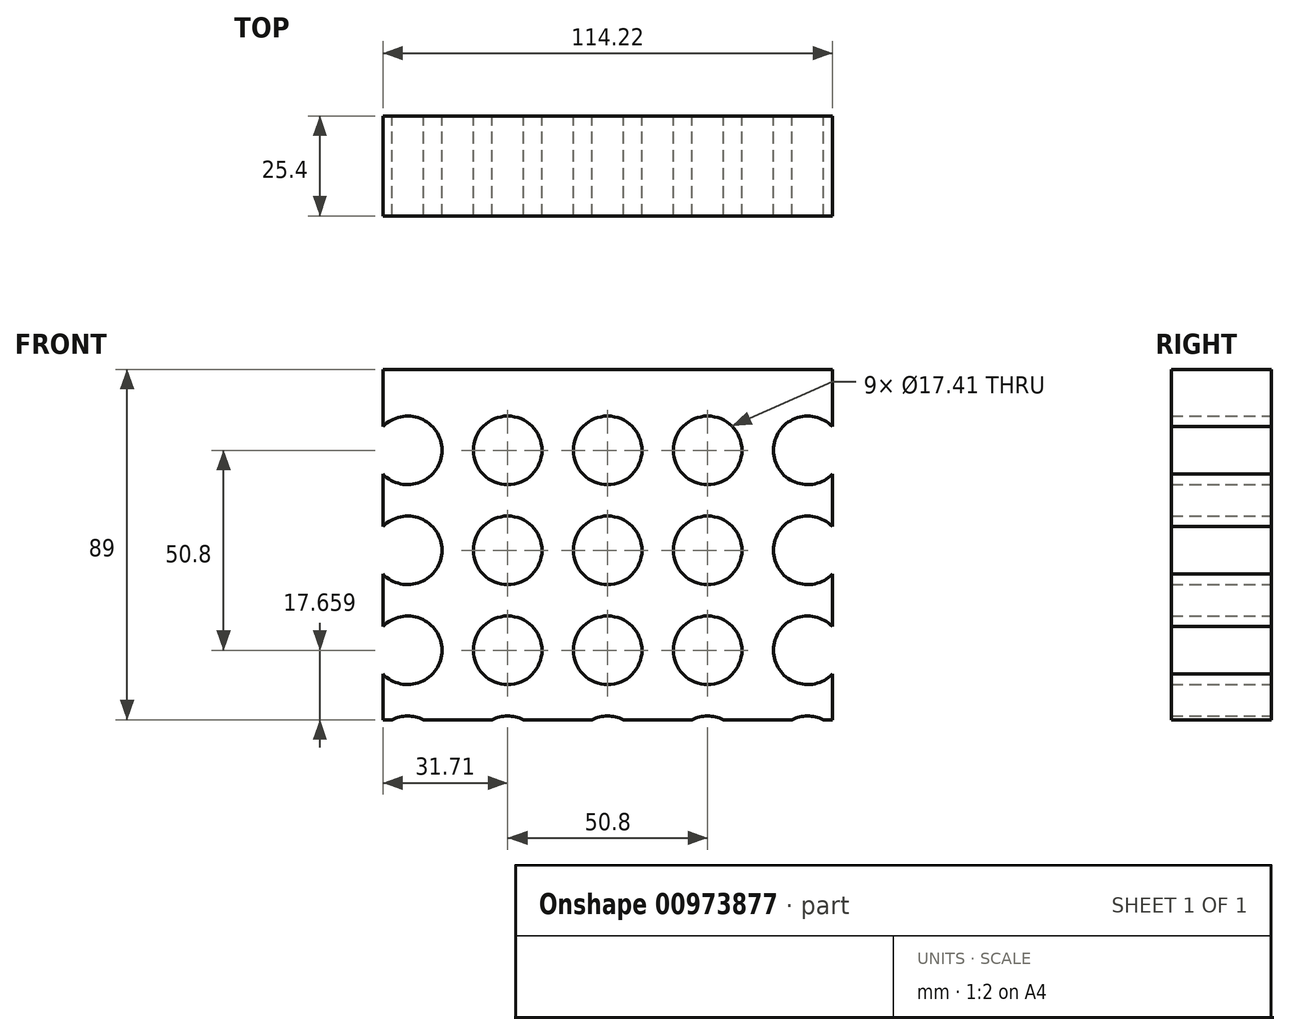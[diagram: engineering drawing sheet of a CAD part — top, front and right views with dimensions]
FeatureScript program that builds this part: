
annotation { "Feature Type Name" : "Feature", "Feature Type Description" : "" }
export const myFeature = defineFeature(function(context is Context, id is Id, definition is map)
    precondition{}
    {
        {
            var Q0;
            Q0=qCreatedBy(makeId("Front.planeOp"),FACE);
            var sketch = newSketch(context, id + "F0", { "sketchPlane" : qUnion([Q0])});
            skLineSegment(sketch, "E0.bottom", {"start": v(57.1, 44.5) * mm, "end": v(-57.1, 44.5) * mm});
            skLineSegment(sketch, "E0.top", {"start": v(57.1, -44.5) * mm, "end": v(-57.1, -44.5) * mm});
            skLineSegment(sketch, "E0.left", {"start": v(57.1, 44.5) * mm, "end": v(57.1, -44.5) * mm});
            skLineSegment(sketch, "E0.right", {"start": v(-57.1, 44.5) * mm, "end": v(-57.1, -44.5) * mm});
            skPoint(sketch, "E0.middle", {"position": v(0, 0) * mm});
            skCircle(sketch, "E1", {"center": v(-25.4, 23.96) * mm, "radius": 8.7 * mm});
            skCircle(sketch, "E2.1.0.0", {"center": v(0, 23.96) * mm, "radius": 8.7 * mm});
            skCircle(sketch, "E2.2.0.0", {"center": v(25.4, 23.96) * mm, "radius": 8.7 * mm});
            skLineSegment(sketch, "E2.direction1", {"start": v(-25.4, 23.96) * mm, "end": v(0, 23.96) * mm, "construction": true});
            skCircle(sketch, "E3.0.3.0", {"center": v(50.8, 23.96) * mm, "radius": 8.7 * mm});
            skCircle(sketch, "E3.0.4.0", {"center": v(76.2, 23.96) * mm, "radius": 8.7 * mm});
            skCircle(sketch, "E3.0.5.0", {"center": v(101.6, 23.96) * mm, "radius": 8.7 * mm});
            skCircle(sketch, "E3.0.6.0", {"center": v(127, 23.96) * mm, "radius": 8.7 * mm});
            skCircle(sketch, "E3.0.7.0", {"center": v(152.4, 23.96) * mm, "radius": 8.7 * mm});
            skCircle(sketch, "E3.0.8.0", {"center": v(177.8, 23.96) * mm, "radius": 8.7 * mm});
            skCircle(sketch, "E3.0.9.0", {"center": v(203.2, 23.96) * mm, "radius": 8.7 * mm});
            skCircle(sketch, "E3.0.10.0", {"center": v(228.6, 23.96) * mm, "radius": 8.7 * mm});
            skCircle(sketch, "E3.0.11.0", {"center": v(254, 23.96) * mm, "radius": 8.7 * mm});
            skCircle(sketch, "E3.0.12.0", {"center": v(279.4, 23.96) * mm, "radius": 8.7 * mm});
            skCircle(sketch, "E3.0.13.0", {"center": v(304.8, 23.96) * mm, "radius": 8.7 * mm});
            skCircle(sketch, "E3.0.14.0", {"center": v(330.2, 23.96) * mm, "radius": 8.7 * mm});
            skLineSegment(sketch, "E4.0.1.0", {"start": v(57.1, 19.1) * mm, "end": v(57.1, -69.9) * mm});
            skCircle(sketch, "E4.0.1.1", {"center": v(-25.4, -1.44) * mm, "radius": 8.7 * mm});
            skCircle(sketch, "E4.0.1.2", {"center": v(0, -1.44) * mm, "radius": 8.7 * mm});
            skPoint(sketch, "E4.0.1.3", {"position": v(0, -25.4) * mm});
            skCircle(sketch, "E4.0.1.4", {"center": v(25.4, -1.44) * mm, "radius": 8.7 * mm});
            skCircle(sketch, "E4.0.1.5", {"center": v(50.8, -1.44) * mm, "radius": 8.7 * mm});
            skCircle(sketch, "E4.0.1.6", {"center": v(76.2, -1.44) * mm, "radius": 8.7 * mm});
            skCircle(sketch, "E4.0.1.7", {"center": v(101.6, -1.44) * mm, "radius": 8.7 * mm});
            skCircle(sketch, "E4.0.1.8", {"center": v(127, -1.44) * mm, "radius": 8.7 * mm});
            skLineSegment(sketch, "E4.0.2.0", {"start": v(57.1, -6.3) * mm, "end": v(57.1, -95.3) * mm});
            skCircle(sketch, "E4.0.2.1", {"center": v(-25.4, -26.84) * mm, "radius": 8.7 * mm});
            skCircle(sketch, "E4.0.2.2", {"center": v(0, -26.84) * mm, "radius": 8.7 * mm});
            skPoint(sketch, "E4.0.2.3", {"position": v(0, -50.8) * mm});
            skCircle(sketch, "E4.0.2.4", {"center": v(25.4, -26.84) * mm, "radius": 8.7 * mm});
            skCircle(sketch, "E4.0.2.5", {"center": v(50.8, -26.84) * mm, "radius": 8.7 * mm});
            skCircle(sketch, "E4.0.2.6", {"center": v(76.2, -26.84) * mm, "radius": 8.7 * mm});
            skCircle(sketch, "E4.0.2.7", {"center": v(101.6, -26.84) * mm, "radius": 8.7 * mm});
            skCircle(sketch, "E4.0.2.8", {"center": v(127, -26.84) * mm, "radius": 8.7 * mm});
            skLineSegment(sketch, "E4.0.3.0", {"start": v(57.1, -31.7) * mm, "end": v(57.1, -120.7) * mm});
            skCircle(sketch, "E4.0.3.1", {"center": v(-25.4, -52.24) * mm, "radius": 8.7 * mm});
            skCircle(sketch, "E4.0.3.2", {"center": v(0, -52.24) * mm, "radius": 8.7 * mm});
            skPoint(sketch, "E4.0.3.3", {"position": v(0, -76.2) * mm});
            skCircle(sketch, "E4.0.3.4", {"center": v(25.4, -52.24) * mm, "radius": 8.7 * mm});
            skCircle(sketch, "E4.0.3.5", {"center": v(50.8, -52.24) * mm, "radius": 8.7 * mm});
            skCircle(sketch, "E4.0.3.6", {"center": v(76.2, -52.24) * mm, "radius": 8.7 * mm});
            skCircle(sketch, "E4.0.3.7", {"center": v(101.6, -52.24) * mm, "radius": 8.7 * mm});
            skCircle(sketch, "E4.0.3.8", {"center": v(127, -52.24) * mm, "radius": 8.7 * mm});
            skLineSegment(sketch, "E4.0.4.0", {"start": v(57.1, -57.1) * mm, "end": v(57.1, -146.1) * mm});
            skCircle(sketch, "E4.0.4.1", {"center": v(-25.4, -77.64) * mm, "radius": 8.7 * mm});
            skCircle(sketch, "E4.0.4.2", {"center": v(0, -77.64) * mm, "radius": 8.7 * mm});
            skPoint(sketch, "E4.0.4.3", {"position": v(0, -101.6) * mm});
            skCircle(sketch, "E4.0.4.4", {"center": v(25.4, -77.64) * mm, "radius": 8.7 * mm});
            skCircle(sketch, "E4.0.4.5", {"center": v(50.8, -77.64) * mm, "radius": 8.7 * mm});
            skCircle(sketch, "E4.0.4.6", {"center": v(76.2, -77.64) * mm, "radius": 8.7 * mm});
            skCircle(sketch, "E4.0.4.7", {"center": v(101.6, -77.64) * mm, "radius": 8.7 * mm});
            skCircle(sketch, "E4.0.4.8", {"center": v(127, -77.64) * mm, "radius": 8.7 * mm});
            skLineSegment(sketch, "E4.1.0.0", {"start": v(31.7, 44.5) * mm, "end": v(31.7, -44.5) * mm});
            skCircle(sketch, "E4.1.0.1", {"center": v(-50.8, 23.96) * mm, "radius": 8.7 * mm});
            skPoint(sketch, "E4.1.0.3", {"position": v(-25.4, 0) * mm});
            skLineSegment(sketch, "E4.1.1.0", {"start": v(31.7, 19.1) * mm, "end": v(31.7, -69.9) * mm});
            skCircle(sketch, "E4.1.1.1", {"center": v(-50.8, -1.44) * mm, "radius": 8.7 * mm});
            skCircle(sketch, "E4.1.1.2", {"center": v(-25.4, -1.44) * mm, "radius": 8.7 * mm});
            skPoint(sketch, "E4.1.1.3", {"position": v(-25.4, -25.4) * mm});
            skCircle(sketch, "E4.1.1.4", {"center": v(0, -1.44) * mm, "radius": 8.7 * mm});
            skCircle(sketch, "E4.1.1.5", {"center": v(25.4, -1.44) * mm, "radius": 8.7 * mm});
            skCircle(sketch, "E4.1.1.6", {"center": v(50.8, -1.44) * mm, "radius": 8.7 * mm});
            skCircle(sketch, "E4.1.1.7", {"center": v(76.2, -1.44) * mm, "radius": 8.7 * mm});
            skCircle(sketch, "E4.1.1.8", {"center": v(101.6, -1.44) * mm, "radius": 8.7 * mm});
            skLineSegment(sketch, "E4.1.2.0", {"start": v(31.7, -6.3) * mm, "end": v(31.7, -95.3) * mm});
            skCircle(sketch, "E4.1.2.1", {"center": v(-50.8, -26.84) * mm, "radius": 8.7 * mm});
            skCircle(sketch, "E4.1.2.2", {"center": v(-25.4, -26.84) * mm, "radius": 8.7 * mm});
            skPoint(sketch, "E4.1.2.3", {"position": v(-25.4, -50.8) * mm});
            skCircle(sketch, "E4.1.2.4", {"center": v(0, -26.84) * mm, "radius": 8.7 * mm});
            skCircle(sketch, "E4.1.2.5", {"center": v(25.4, -26.84) * mm, "radius": 8.7 * mm});
            skCircle(sketch, "E4.1.2.6", {"center": v(50.8, -26.84) * mm, "radius": 8.7 * mm});
            skCircle(sketch, "E4.1.2.7", {"center": v(76.2, -26.84) * mm, "radius": 8.7 * mm});
            skCircle(sketch, "E4.1.2.8", {"center": v(101.6, -26.84) * mm, "radius": 8.7 * mm});
            skLineSegment(sketch, "E4.1.3.0", {"start": v(31.7, -31.7) * mm, "end": v(31.7, -120.7) * mm});
            skCircle(sketch, "E4.1.3.1", {"center": v(-50.8, -52.24) * mm, "radius": 8.7 * mm});
            skCircle(sketch, "E4.1.3.2", {"center": v(-25.4, -52.24) * mm, "radius": 8.7 * mm});
            skPoint(sketch, "E4.1.3.3", {"position": v(-25.4, -76.2) * mm});
            skCircle(sketch, "E4.1.3.4", {"center": v(0, -52.24) * mm, "radius": 8.7 * mm});
            skCircle(sketch, "E4.1.3.5", {"center": v(25.4, -52.24) * mm, "radius": 8.7 * mm});
            skCircle(sketch, "E4.1.3.6", {"center": v(50.8, -52.24) * mm, "radius": 8.7 * mm});
            skCircle(sketch, "E4.1.3.7", {"center": v(76.2, -52.24) * mm, "radius": 8.7 * mm});
            skCircle(sketch, "E4.1.3.8", {"center": v(101.6, -52.24) * mm, "radius": 8.7 * mm});
            skLineSegment(sketch, "E4.1.4.0", {"start": v(31.7, -57.1) * mm, "end": v(31.7, -146.1) * mm});
            skCircle(sketch, "E4.1.4.1", {"center": v(-50.8, -77.64) * mm, "radius": 8.7 * mm});
            skCircle(sketch, "E4.1.4.2", {"center": v(-25.4, -77.64) * mm, "radius": 8.7 * mm});
            skPoint(sketch, "E4.1.4.3", {"position": v(-25.4, -101.6) * mm});
            skCircle(sketch, "E4.1.4.4", {"center": v(0, -77.64) * mm, "radius": 8.7 * mm});
            skCircle(sketch, "E4.1.4.5", {"center": v(25.4, -77.64) * mm, "radius": 8.7 * mm});
            skCircle(sketch, "E4.1.4.6", {"center": v(50.8, -77.64) * mm, "radius": 8.7 * mm});
            skCircle(sketch, "E4.1.4.7", {"center": v(76.2, -77.64) * mm, "radius": 8.7 * mm});
            skCircle(sketch, "E4.1.4.8", {"center": v(101.6, -77.64) * mm, "radius": 8.7 * mm});
            skLineSegment(sketch, "E4.2.0.0", {"start": v(6.3, 44.5) * mm, "end": v(6.3, -44.5) * mm});
            skCircle(sketch, "E4.2.0.1", {"center": v(-76.2, 23.96) * mm, "radius": 8.7 * mm});
            skCircle(sketch, "E4.2.0.2", {"center": v(-50.8, 23.96) * mm, "radius": 8.7 * mm});
            skPoint(sketch, "E4.2.0.3", {"position": v(-50.8, 0) * mm});
            skLineSegment(sketch, "E4.2.1.0", {"start": v(6.3, 19.1) * mm, "end": v(6.3, -69.9) * mm});
            skCircle(sketch, "E4.2.1.1", {"center": v(-76.2, -1.44) * mm, "radius": 8.7 * mm});
            skCircle(sketch, "E4.2.1.2", {"center": v(-50.8, -1.44) * mm, "radius": 8.7 * mm});
            skPoint(sketch, "E4.2.1.3", {"position": v(-50.8, -25.4) * mm});
            skCircle(sketch, "E4.2.1.4", {"center": v(-25.4, -1.44) * mm, "radius": 8.7 * mm});
            skCircle(sketch, "E4.2.1.5", {"center": v(0, -1.44) * mm, "radius": 8.7 * mm});
            skCircle(sketch, "E4.2.1.6", {"center": v(25.4, -1.44) * mm, "radius": 8.7 * mm});
            skCircle(sketch, "E4.2.1.7", {"center": v(50.8, -1.44) * mm, "radius": 8.7 * mm});
            skCircle(sketch, "E4.2.1.8", {"center": v(76.2, -1.44) * mm, "radius": 8.7 * mm});
            skLineSegment(sketch, "E4.2.2.0", {"start": v(6.3, -6.3) * mm, "end": v(6.3, -95.3) * mm});
            skCircle(sketch, "E4.2.2.1", {"center": v(-76.2, -26.84) * mm, "radius": 8.7 * mm});
            skCircle(sketch, "E4.2.2.2", {"center": v(-50.8, -26.84) * mm, "radius": 8.7 * mm});
            skPoint(sketch, "E4.2.2.3", {"position": v(-50.8, -50.8) * mm});
            skCircle(sketch, "E4.2.2.4", {"center": v(-25.4, -26.84) * mm, "radius": 8.7 * mm});
            skCircle(sketch, "E4.2.2.5", {"center": v(0, -26.84) * mm, "radius": 8.7 * mm});
            skCircle(sketch, "E4.2.2.6", {"center": v(25.4, -26.84) * mm, "radius": 8.7 * mm});
            skCircle(sketch, "E4.2.2.7", {"center": v(50.8, -26.84) * mm, "radius": 8.7 * mm});
            skCircle(sketch, "E4.2.2.8", {"center": v(76.2, -26.84) * mm, "radius": 8.7 * mm});
            skLineSegment(sketch, "E4.2.3.0", {"start": v(6.3, -31.7) * mm, "end": v(6.3, -120.7) * mm});
            skCircle(sketch, "E4.2.3.1", {"center": v(-76.2, -52.24) * mm, "radius": 8.7 * mm});
            skCircle(sketch, "E4.2.3.2", {"center": v(-50.8, -52.24) * mm, "radius": 8.7 * mm});
            skPoint(sketch, "E4.2.3.3", {"position": v(-50.8, -76.2) * mm});
            skCircle(sketch, "E4.2.3.4", {"center": v(-25.4, -52.24) * mm, "radius": 8.7 * mm});
            skCircle(sketch, "E4.2.3.5", {"center": v(0, -52.24) * mm, "radius": 8.7 * mm});
            skCircle(sketch, "E4.2.3.6", {"center": v(25.4, -52.24) * mm, "radius": 8.7 * mm});
            skCircle(sketch, "E4.2.3.7", {"center": v(50.8, -52.24) * mm, "radius": 8.7 * mm});
            skCircle(sketch, "E4.2.3.8", {"center": v(76.2, -52.24) * mm, "radius": 8.7 * mm});
            skLineSegment(sketch, "E4.2.4.0", {"start": v(6.3, -57.1) * mm, "end": v(6.3, -146.1) * mm});
            skCircle(sketch, "E4.2.4.1", {"center": v(-76.2, -77.64) * mm, "radius": 8.7 * mm});
            skCircle(sketch, "E4.2.4.2", {"center": v(-50.8, -77.64) * mm, "radius": 8.7 * mm});
            skPoint(sketch, "E4.2.4.3", {"position": v(-50.8, -101.6) * mm});
            skCircle(sketch, "E4.2.4.4", {"center": v(-25.4, -77.64) * mm, "radius": 8.7 * mm});
            skCircle(sketch, "E4.2.4.5", {"center": v(0, -77.64) * mm, "radius": 8.7 * mm});
            skCircle(sketch, "E4.2.4.6", {"center": v(25.4, -77.64) * mm, "radius": 8.7 * mm});
            skCircle(sketch, "E4.2.4.7", {"center": v(50.8, -77.64) * mm, "radius": 8.7 * mm});
            skCircle(sketch, "E4.2.4.8", {"center": v(76.2, -77.64) * mm, "radius": 8.7 * mm});
            skLineSegment(sketch, "E4.direction1", {"start": v(-25.4, 23.96) * mm, "end": v(-50.8, 23.96) * mm, "construction": true});
            skLineSegment(sketch, "E4.direction2", {"start": v(-25.4, 23.96) * mm, "end": v(-25.4, -1.44) * mm, "construction": true});
            skSolve(sketch);
        }
        {
            var Q0;
            {var subQ11=sQuery(id+"F0.wireOp",EDGE,"E0.bottom");var subQ18=sQuery(id+"F0.wireOp",EDGE,"E0.left");var subQ19=makeQuery(id+"F0.imprint","INTERSECT",VERTEX,{"derivedFrom":[subQ11,subQ18]});Q0=makeQuery(id+"F0.imprint","IMPRINT",FACE,{"disambiguationData":[TD([[makeQuery(id+"F0.imprint","IMPRINT",EDGE,{"disambiguationData":[TD([[subQ19,-1.0]])],"derivedFrom":subQ11}),1.0]])]});}
            var Q1;
            {var subQ1=sQuery(id+"F0.wireOp",EDGE,"E4.1.0.0");var subQ17=sQuery(id+"F0.wireOp",EDGE,"E0.bottom");var subQ30=makeQuery(id+"F0.imprint","INTERSECT",VERTEX,{"derivedFrom":[subQ17,subQ1]});Q1=makeQuery(id+"F0.imprint","IMPRINT",FACE,{"disambiguationData":[TD([[makeQuery(id+"F0.imprint","IMPRINT",EDGE,{"disambiguationData":[TD([[subQ30,-1.0]])],"derivedFrom":subQ17}),1.0]])]});}
            var Q2;
            Q2=makeQuery(id+"F0.imprint","IMPRINT",FACE,{"disambiguationData":[TD([[makeQuery(id+"F0.imprint","IMPRINT",EDGE,{"derivedFrom":sQuery(id+"F0.wireOp",EDGE,"E1")}),-1.0]])]});
            extrude(context, id + "F1", {"entities" : qUnion([Q0, Q1, Q2]), "depth" : 25.4 * mm, "offsetDistance" : 25.4 * mm});
        }
    });
